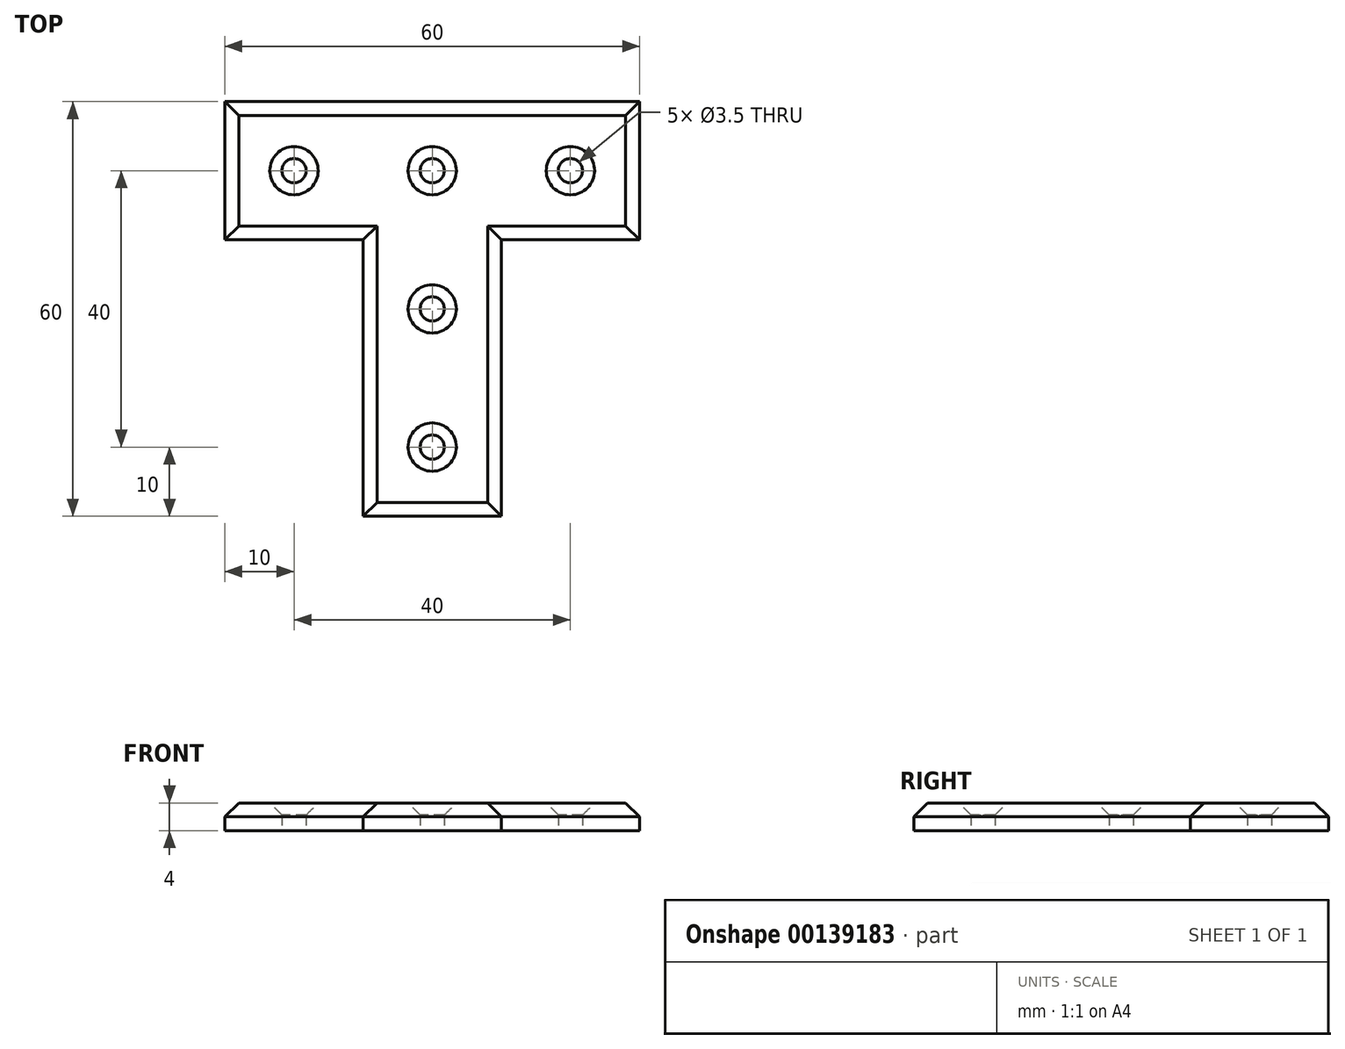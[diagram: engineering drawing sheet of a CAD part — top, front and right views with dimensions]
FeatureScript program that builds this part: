
annotation { "Feature Type Name" : "Feature", "Feature Type Description" : "" }
export const myFeature = defineFeature(function(context is Context, id is Id, definition is map)
    precondition{}
    {
        {
            var Q0;
            Q0=qCreatedBy(makeId("Top.planeOp"),FACE);
            var sketch = newSketch(context, id + "F0", { "sketchPlane" : qUnion([Q0])});
            skLineSegment(sketch, "E0", {"start": v(0, -50) * mm, "end": v(10, -50) * mm});
            skLineSegment(sketch, "E1", {"start": v(10, -50) * mm, "end": v(10, -10) * mm});
            skLineSegment(sketch, "E2", {"start": v(10, -10) * mm, "end": v(50, -10) * mm});
            skLineSegment(sketch, "E3", {"start": v(50, -10) * mm, "end": v(50, 10) * mm});
            skLineSegment(sketch, "E4", {"start": v(50, 10) * mm, "end": v(0, 10) * mm});
            skLineSegment(sketch, "E5.MirrorCS", {"start": v(-10, -50) * mm, "end": v(-10, -10) * mm});
            skLineSegment(sketch, "E6.MirrorCS", {"start": v(0, -50) * mm, "end": v(-10, -50) * mm});
            skLineSegment(sketch, "E7.MirrorCS", {"start": v(-50, -10) * mm, "end": v(-50, 10) * mm});
            skLineSegment(sketch, "E8.MirrorCS", {"start": v(-10, -10) * mm, "end": v(-50, -10) * mm});
            skLineSegment(sketch, "E9.MirrorCS", {"start": v(-50, 10) * mm, "end": v(0, 10) * mm});
            skCircle(sketch, "E10", {"center": v(0, 0) * mm, "radius": 1.75 * mm});
            skCircle(sketch, "E11", {"center": v(20, 0) * mm, "radius": 1.75 * mm});
            skCircle(sketch, "E12", {"center": v(40, 0) * mm, "radius": 1.75 * mm});
            skCircle(sketch, "E13", {"center": v(0, -20) * mm, "radius": 1.75 * mm});
            skCircle(sketch, "E14", {"center": v(0, -40) * mm, "radius": 1.75 * mm});
            skCircle(sketch, "E15.MirrorC", {"center": v(-40, 0) * mm, "radius": 1.75 * mm});
            skCircle(sketch, "E16.MirrorC", {"center": v(-20, 0) * mm, "radius": 1.75 * mm});
            skLineSegment(sketch, "E17", {"start": v(-30, -10) * mm, "end": v(-30, 10) * mm});
            skLineSegment(sketch, "E18", {"start": v(30, -10) * mm, "end": v(30, 10) * mm});
            skSolve(sketch);
        }
        {
            var Q0;
            Q0=makeQuery(id+"F0.imprint","IMPRINT",FACE,{"disambiguationData":[TD([[makeQuery(id+"F0.imprint","IMPRINT",EDGE,{"derivedFrom":sQuery(id+"F0.wireOp",EDGE,"E0")}),1.0]])]});
            extrude(context, id + "F1", {"entities" : qUnion([Q0]), "depth" : 4 * mm});
        }
        {
            var Q0;
            Q0=makeQuery(id+"F1.opExtrude","CAP_EDGE",EDGE,{"disambiguationData":[OSD([sQuery(id+"F0.wireOp",EDGE,"E0"),sQuery(id+"F0.wireOp",EDGE,"E6.MirrorCS")])],"isStart":false});
            var Q1;
            Q1=makeQuery(id+"F1.opExtrude","CAP_EDGE",EDGE,{"disambiguationData":[OSD([sQuery(id+"F0.wireOp",EDGE,"E1")])],"isStart":false});
            var Q2;
            Q2=makeQuery(id+"F1.opExtrude","CAP_EDGE",EDGE,{"disambiguationData":[OSD([sQuery(id+"F0.wireOp",EDGE,"E2")])],"isStart":false});
            var Q3;
            Q3=makeQuery(id+"F1.opExtrude","CAP_EDGE",EDGE,{"disambiguationData":[OSD([sQuery(id+"F0.wireOp",EDGE,"E3")])],"isStart":false});
            var Q4;
            Q4=makeQuery(id+"F1.opExtrude","CAP_EDGE",EDGE,{"disambiguationData":[OSD([sQuery(id+"F0.wireOp",EDGE,"E4"),sQuery(id+"F0.wireOp",EDGE,"E9.MirrorCS")])],"isStart":false});
            var Q5;
            Q5=makeQuery(id+"F1.opExtrude","CAP_EDGE",EDGE,{"disambiguationData":[OSD([sQuery(id+"F0.wireOp",EDGE,"E7.MirrorCS")])],"isStart":false});
            var Q6;
            Q6=makeQuery(id+"F1.opExtrude","CAP_EDGE",EDGE,{"disambiguationData":[OSD([sQuery(id+"F0.wireOp",EDGE,"E8.MirrorCS")])],"isStart":false});
            var Q7;
            Q7=makeQuery(id+"F1.opExtrude","CAP_EDGE",EDGE,{"disambiguationData":[OSD([sQuery(id+"F0.wireOp",EDGE,"E5.MirrorCS")])],"isStart":false});
            var Q8;
            Q8=makeQuery(id+"F1.opExtrude","CAP_EDGE",EDGE,{"disambiguationData":[OSD([sQuery(id+"F0.wireOp",EDGE,"E17")])],"isStart":false});
            var Q9;
            Q9=makeQuery(id+"F1.opExtrude","CAP_EDGE",EDGE,{"disambiguationData":[OSD([sQuery(id+"F0.wireOp",EDGE,"E18")])],"isStart":false});
            chamfer(context, id + "F2", {"entities" : qUnion([Q0, Q1, Q2, Q3, Q4, Q5, Q6, Q7, Q8, Q9]), "width" : 2 * mm, "tangentPropagation" : true});
        }
        {
            var Q0;
            Q0=makeQuery(id+"F1.opExtrude","CAP_EDGE",EDGE,{"disambiguationData":[OSD([sQuery(id+"F0.wireOp",EDGE,"E15.MirrorC")])],"isStart":false});
            var Q1;
            Q1=makeQuery(id+"F1.opExtrude","CAP_EDGE",EDGE,{"disambiguationData":[OSD([sQuery(id+"F0.wireOp",EDGE,"E16.MirrorC")])],"isStart":false});
            var Q2;
            Q2=makeQuery(id+"F1.opExtrude","CAP_EDGE",EDGE,{"disambiguationData":[OSD([sQuery(id+"F0.wireOp",EDGE,"E10")])],"isStart":false});
            var Q3;
            Q3=makeQuery(id+"F1.opExtrude","CAP_EDGE",EDGE,{"disambiguationData":[OSD([sQuery(id+"F0.wireOp",EDGE,"E11")])],"isStart":false});
            var Q4;
            Q4=makeQuery(id+"F1.opExtrude","CAP_EDGE",EDGE,{"disambiguationData":[OSD([sQuery(id+"F0.wireOp",EDGE,"E12")])],"isStart":false});
            var Q5;
            Q5=makeQuery(id+"F1.opExtrude","CAP_EDGE",EDGE,{"disambiguationData":[OSD([sQuery(id+"F0.wireOp",EDGE,"E13")])],"isStart":false});
            var Q6;
            Q6=makeQuery(id+"F1.opExtrude","CAP_EDGE",EDGE,{"disambiguationData":[OSD([sQuery(id+"F0.wireOp",EDGE,"E14")])],"isStart":false});
            chamfer(context, id + "F3", {"entities" : qUnion([Q0, Q1, Q2, Q3, Q4, Q5, Q6]), "width" : 1.75 * mm, "tangentPropagation" : true});
        }
    });
